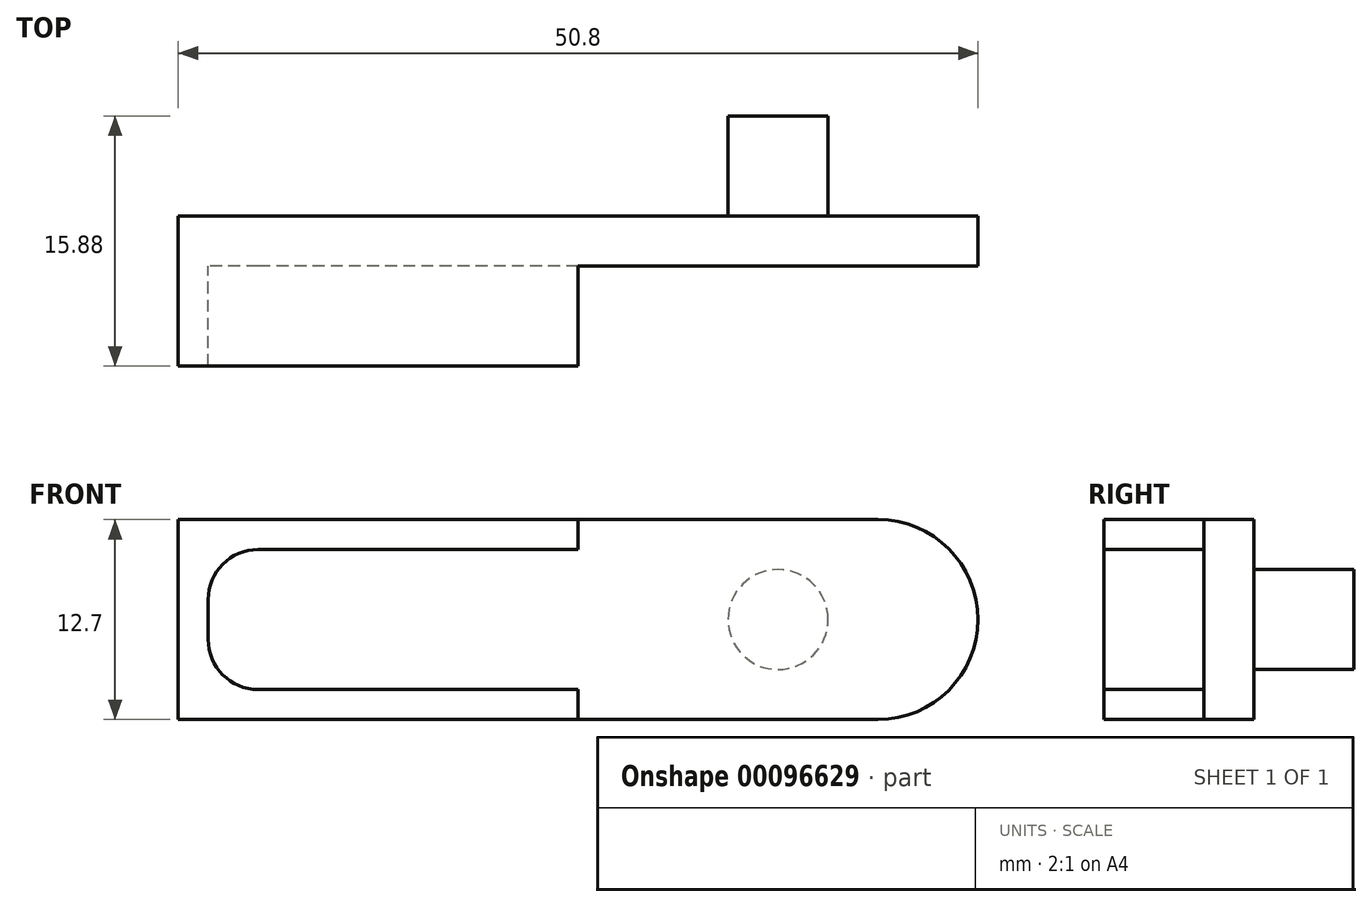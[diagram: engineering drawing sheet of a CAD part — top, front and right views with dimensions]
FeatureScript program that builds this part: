
annotation { "Feature Type Name" : "Feature", "Feature Type Description" : "" }
export const myFeature = defineFeature(function(context is Context, id is Id, definition is map)
    precondition{}
    {
        {
            var Q0;
            Q0=qCreatedBy(makeId("Front.planeOp"),FACE);
            var sketch = newSketch(context, id + "F0", { "sketchPlane" : qUnion([Q0])});
            skLineSegment(sketch, "E0.bottom", {"start": v(-23.41, -5.67) * mm, "end": v(27.39, -5.67) * mm});
            skLineSegment(sketch, "E0.top", {"start": v(-23.41, -18.37) * mm, "end": v(27.39, -18.37) * mm});
            skLineSegment(sketch, "E0.left", {"start": v(-23.41, -5.67) * mm, "end": v(-23.41, -18.37) * mm});
            skLineSegment(sketch, "E0.right", {"start": v(27.39, -5.67) * mm, "end": v(27.39, -18.37) * mm});
            skSolve(sketch);
        }
        {
            var Q0;
            Q0=makeQuery(id+"F0.imprint","IMPRINT",FACE,{"disambiguationData":[TD([[makeQuery(id+"F0.imprint","IMPRINT",EDGE,{"derivedFrom":sQuery(id+"F0.wireOp",EDGE,"E0.bottom")}),-1.0]])]});
            extrude(context, id + "F1", {"entities" : qUnion([Q0]), "depth" : 3.17 * mm});
        }
        {
            var Q0;
            Q0=makeQuery(id+"F1.opExtrude","CAP_FACE",FACE,{"disambiguationData":[OSD([sQuery(id+"F0.wireOp",EDGE,"E0.bottom"),sQuery(id+"F0.wireOp",EDGE,"E0.top"),sQuery(id+"F0.wireOp",EDGE,"E0.left"),sQuery(id+"F0.wireOp",EDGE,"E0.right")])],"isStart":true});
            var sketch = newSketch(context, id + "F2", { "sketchPlane" : qUnion([Q0])});
            skCircle(sketch, "E1", {"center": v(-14.69, -12.02) * mm, "radius": 3.18 * mm});
            skPoint(sketch, "E1.centerSnap0", {"position": v(-27.39, -12.02) * mm});
            skSolve(sketch);
        }
        {
            var Q0;
            Q0=makeQuery(id+"F2.imprint","IMPRINT",FACE,{"disambiguationData":[TD([[makeQuery(id+"F2.imprint","IMPRINT",EDGE,{"derivedFrom":sQuery(id+"F2.wireOp",EDGE,"E1")}),1.0]])]});
            extrude(context, id + "F3", {"entities" : qUnion([Q0]), "operationType" : NewBodyOperationType.ADD, "depth" : 6.35 * mm});
        }
        {
            var Q0;
            Q0=makeQuery(id+"F1.opExtrude","CAP_FACE",FACE,{"disambiguationData":[OSD([sQuery(id+"F0.wireOp",EDGE,"E0.bottom"),sQuery(id+"F0.wireOp",EDGE,"E0.top"),sQuery(id+"F0.wireOp",EDGE,"E0.left"),sQuery(id+"F0.wireOp",EDGE,"E0.right")])],"isStart":false});
            var sketch = newSketch(context, id + "F4", { "sketchPlane" : qUnion([Q0])});
            skLineSegment(sketch, "E2", {"start": v(-23.41, -5.67) * mm, "end": v(1.99, -5.67) * mm});
            skLineSegment(sketch, "E3", {"start": v(1.99, -5.67) * mm, "end": v(1.99, -7.58) * mm});
            skLineSegment(sketch, "E4", {"start": v(1.99, -7.58) * mm, "end": v(-21.5, -7.58) * mm});
            skLineSegment(sketch, "E5", {"start": v(-21.5, -7.58) * mm, "end": v(-21.5, -16.47) * mm});
            skLineSegment(sketch, "E6", {"start": v(-21.5, -16.47) * mm, "end": v(1.99, -16.47) * mm});
            skLineSegment(sketch, "E7", {"start": v(1.99, -16.47) * mm, "end": v(1.99, -18.37) * mm});
            skLineSegment(sketch, "E8", {"start": v(1.99, -18.37) * mm, "end": v(-23.41, -18.37) * mm});
            skLineSegment(sketch, "E9", {"start": v(-23.41, -18.37) * mm, "end": v(-23.41, -5.67) * mm});
            skSolve(sketch);
        }
        {
            var Q0;
            Q0 = qSketchRegion(id + "F4", true);
            extrude(context, id + "F5", {"entities" : qUnion([Q0]), "operationType" : NewBodyOperationType.ADD, "depth" : 6.35 * mm});
        }
        {
            var Q0;
            Q0=makeQuery(id+"F5.opExtrude","SWEPT_EDGE",EDGE,{"disambiguationData":[OSD([sQuery(id+"F4.wireOp",EDGE,"E4"),sQuery(id+"F4.wireOp",EDGE,"E5")])]});
            var Q1;
            Q1=makeQuery(id+"F5.opExtrude","SWEPT_EDGE",EDGE,{"disambiguationData":[OSD([sQuery(id+"F4.wireOp",EDGE,"E5"),sQuery(id+"F4.wireOp",EDGE,"E6")])]});
            fillet(context, id + "F6", {"entities" : qUnion([Q0, Q1]), "radius" : 3.17 * mm, "tangentPropagation" : true, "allowEdgeOverflow" : false});
        }
        {
            var Q0;
            Q0=makeQuery(id+"F1.opExtrude","SWEPT_EDGE",EDGE,{"disambiguationData":[OSD([sQuery(id+"F0.wireOp",EDGE,"E0.bottom"),sQuery(id+"F0.wireOp",EDGE,"E0.right")])]});
            var Q1;
            Q1=makeQuery(id+"F1.opExtrude","SWEPT_EDGE",EDGE,{"disambiguationData":[OSD([sQuery(id+"F0.wireOp",EDGE,"E0.top"),sQuery(id+"F0.wireOp",EDGE,"E0.right")])]});
            fillet(context, id + "F7", {"entities" : qUnion([Q0, Q1]), "radius" : 6.35 * mm, "tangentPropagation" : true, "allowEdgeOverflow" : false});
        }
    });
